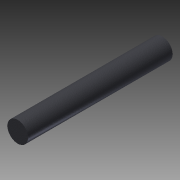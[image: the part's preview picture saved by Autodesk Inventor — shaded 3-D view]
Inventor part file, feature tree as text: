
AUTODESK INVENTOR PART (.ipt)
format: ipt  version: 2013 (Build 170138000, 138)  size: 87,552 bytes
history: native  units: in
note: dims shown in document units (in); Inventor stores cm internally (conversion verified against a paired STEP export)
features: extrude x1, sketch x1
ambient origin geometry x8: Origin, YZ Plane, XZ Plane, XY Plane, X Axis, Y Axis, Z Axis, Center Point
bodies: Solid1 (feature_tree)
feature tree (2):
  extrude  "Extrusion1"  Depth=14.0in TaperAngle=0.0deg
  sketch  "Sketch1"  dims[d0=2.0in d1=14.0in d2=0.0in]
